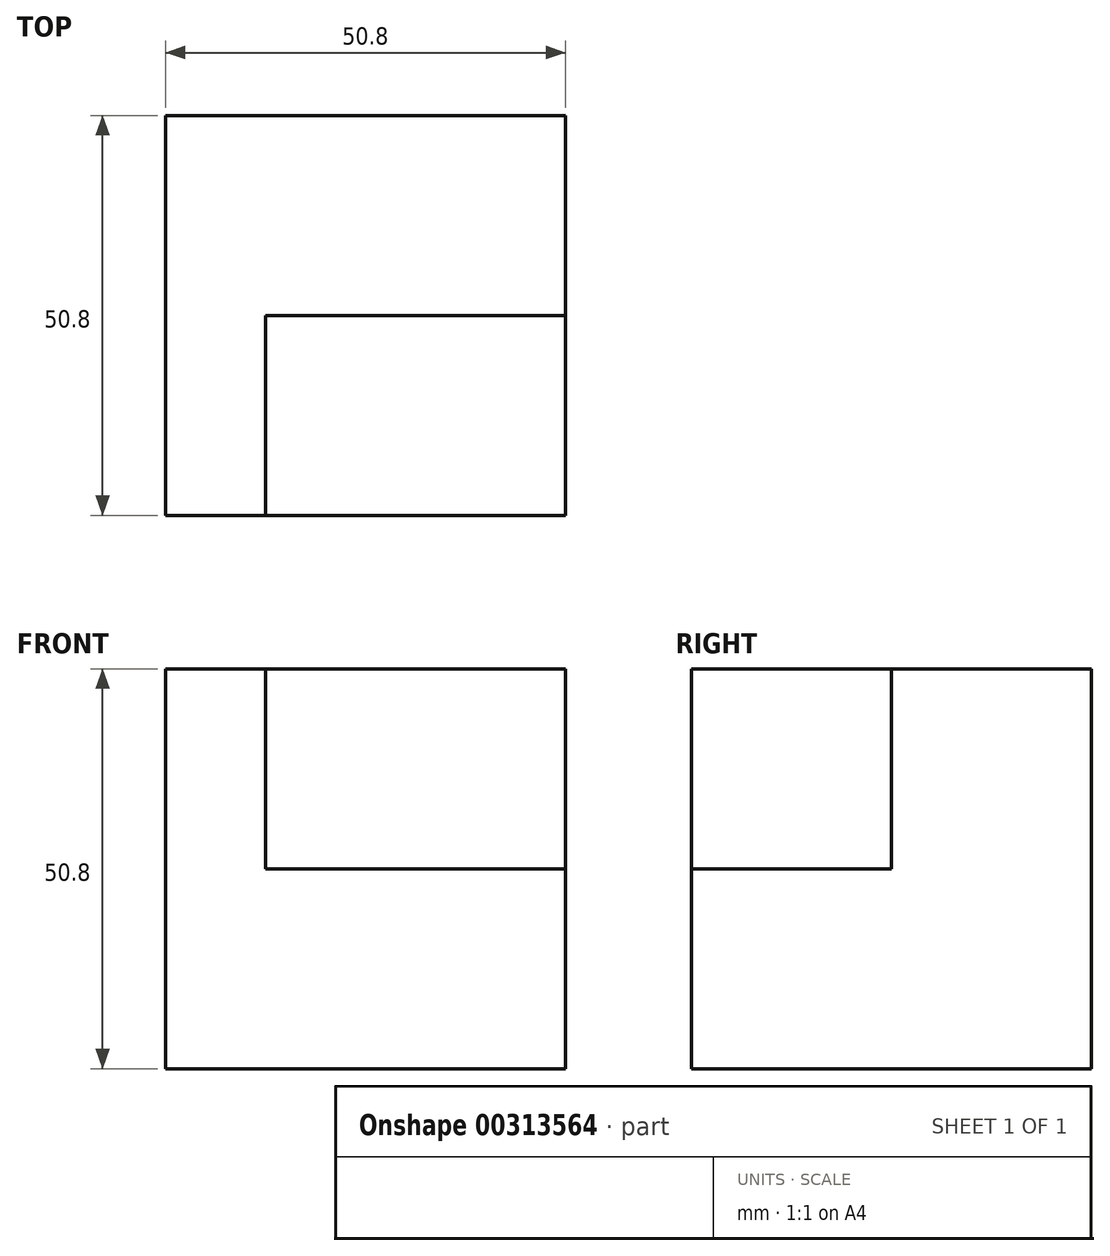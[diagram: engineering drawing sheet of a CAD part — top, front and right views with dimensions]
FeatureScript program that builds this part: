
annotation { "Feature Type Name" : "Feature", "Feature Type Description" : "" }
export const myFeature = defineFeature(function(context is Context, id is Id, definition is map)
    precondition{}
    {
        {
            var Q0;
            Q0=qCreatedBy(makeId("Front.planeOp"),FACE);
            var sketch = newSketch(context, id + "F0", { "sketchPlane" : qUnion([Q0])});
            skLineSegment(sketch, "E0", {"start": v(-30.2, -39.15) * mm, "end": v(20.6, -39.15) * mm});
            skLineSegment(sketch, "E1", {"start": v(-30.2, -39.15) * mm, "end": v(-30.2, 11.65) * mm});
            skLineSegment(sketch, "E2", {"start": v(20.6, -39.15) * mm, "end": v(20.6, -13.75) * mm});
            skLineSegment(sketch, "E3", {"start": v(20.6, -13.75) * mm, "end": v(-17.5, -13.75) * mm});
            skLineSegment(sketch, "E4", {"start": v(-17.5, -13.75) * mm, "end": v(-17.5, 11.65) * mm});
            skLineSegment(sketch, "E5", {"start": v(-17.5, 11.65) * mm, "end": v(-30.2, 11.65) * mm});
            skSolve(sketch);
        }
        {
            var Q0;
            Q0=makeQuery(id+"F0.imprint","IMPRINT",FACE,{"disambiguationData":[TD([[makeQuery(id+"F0.imprint","IMPRINT",EDGE,{"derivedFrom":sQuery(id+"F0.wireOp",EDGE,"E0")}),1.0]])]});
            extrude(context, id + "F1", {"entities" : qUnion([Q0]), "depth" : 50.8 * mm});
        }
        {
            var Q0;
            Q0=makeQuery(id+"F1.opExtrude","CAP_FACE",FACE,{"disambiguationData":[OSD([sQuery(id+"F0.wireOp",EDGE,"E0"),sQuery(id+"F0.wireOp",EDGE,"E1"),sQuery(id+"F0.wireOp",EDGE,"E2"),sQuery(id+"F0.wireOp",EDGE,"E3"),sQuery(id+"F0.wireOp",EDGE,"E4"),sQuery(id+"F0.wireOp",EDGE,"E5")])],"isStart":true});
            var sketch = newSketch(context, id + "F2", { "sketchPlane" : qUnion([Q0])});
            skLineSegment(sketch, "E6", {"start": v(17.5, 11.65) * mm, "end": v(-20.6, 11.65) * mm});
            skLineSegment(sketch, "E7", {"start": v(-20.6, 11.65) * mm, "end": v(-20.6, -13.75) * mm});
            skSolve(sketch);
        }
        {
            var Q0;
            Q0=makeQuery(id+"F2.imprint","IMPRINT",FACE,{"disambiguationData":[TD([[makeQuery(id+"F2.imprint","IMPRINT",EDGE,{"derivedFrom":sQuery(id+"F2.wireOp",EDGE,"E6")}),1.0]])]});
            extrude(context, id + "F3", {"entities" : qUnion([Q0]), "operationType" : NewBodyOperationType.ADD, "depth" : -25.4 * mm});
        }
    });
